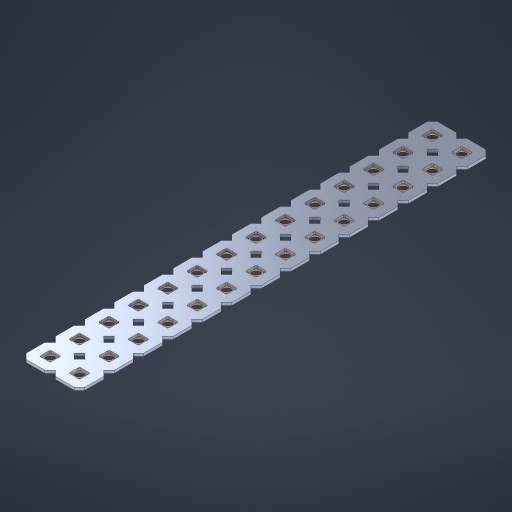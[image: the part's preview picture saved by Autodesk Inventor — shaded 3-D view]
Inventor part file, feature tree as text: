
AUTODESK INVENTOR PART (.ipt)
format: ipt  version: 2023 (Build 270158000, 158)  size: 575,488 bytes
history: native  units: in
note: dims shown in document units (in); Inventor stores cm internally (conversion verified against a paired STEP export)
features: other x29, extrude x27, sketch x2, pattern_linear x1
ambient origin geometry x8: Origin, YZ Plane, XZ Plane, XY Plane, X Axis, Y Axis, Z Axis, Center Point
bodies: Solid1 (feature_tree), Body (feature_tree)
feature tree (59):
  pattern_linear  "Rectangular Pattern1"  Spacing1=0.09in  [1 undecoded]
  sketch  "Sketch1"  dims[d1=0.5in]
  sketch  "Sketch2"  dims[d2=0.182in d3=0.09in d4=0.09in d5=0.09in d6=0.09in d7=0.09in d8=0.09in d9=0.09in d10=0.09in d11=0.02in d13=0.0in d14=0.172in d15=0.0625in d16=0.0in d19=0.5in d22=0.5in]
  other  "Srf1"
  other  "Srf126"
  other  "Srf127"
  other  "Srf128"
  other  "Srf129"
  other  "Srf130"
  other  "Srf131"
  other  "Srf250"
  other  "Srf251"
  other  "Srf252"
  other  "Srf253"
  other  "Srf254"
  other  "Srf255"
  other  "Srf256"
  other  "Srf268"
  other  "Srf269"
  other  "Srf270"
  other  "Srf271"
  other  "Srf272"
  other  "Srf273"
  other  "Srf274"
  other  "Srf275"
  other  "Srf276"
  other  "Srf277"
  other  "Srf278"
  other  "Srf279"
  other  "Srf280"
  other  "Srf281"
  other  "Circle"
  extrude  "ExtrusionSrf126"  Depth=0.09in
  extrude  "ExtrusionSrf127"  Depth=0.09in
  extrude  "ExtrusionSrf128"  Depth=0.09in
  extrude  "ExtrusionSrf129"  Depth=0.09in
  extrude  "ExtrusionSrf130"  Depth=0.09in
  extrude  "ExtrusionSrf131"  Depth=0.09in
  extrude  "ExtrusionSrf250"  Depth=0.09in
  extrude  "ExtrusionSrf251"  Depth=0.02in
  extrude  "ExtrusionSrf252"  TaperAngle=0.0deg  [1 undecoded]
  extrude  "ExtrusionSrf253"  Depth=0.5in
  extrude  "ExtrusionSrf254"  Depth=0.5in TaperAngle=0.0deg
  extrude  "ExtrusionSrf255"  Depth=0.5in
  extrude  "ExtrusionSrf256"  Depth=0.5in
  extrude  "ExtrusionSrf268"  [1 undecoded]
  extrude  "ExtrusionSrf269"  [1 undecoded]
  extrude  "ExtrusionSrf270"  [1 undecoded]
  extrude  "ExtrusionSrf271"  [1 undecoded]
  extrude  "ExtrusionSrf272"  [1 undecoded]
  extrude  "ExtrusionSrf273"  [1 undecoded]
  extrude  "ExtrusionSrf274"  [1 undecoded]
  extrude  "ExtrusionSrf275"  [1 undecoded]
  extrude  "ExtrusionSrf276"  [1 undecoded]
  extrude  "ExtrusionSrf277"  [1 undecoded]
  extrude  "ExtrusionSrf278"  [1 undecoded]
  extrude  "ExtrusionSrf279"  [1 undecoded]
  extrude  "ExtrusionSrf280"  [1 undecoded]
  extrude  "ExtrusionSrf281"  [1 undecoded]
note: 16 required parameter values undecoded (feature->parameter linkage not recoverable at this tier; creation-order binding heuristic only, values carry confidence <= 0.55)
